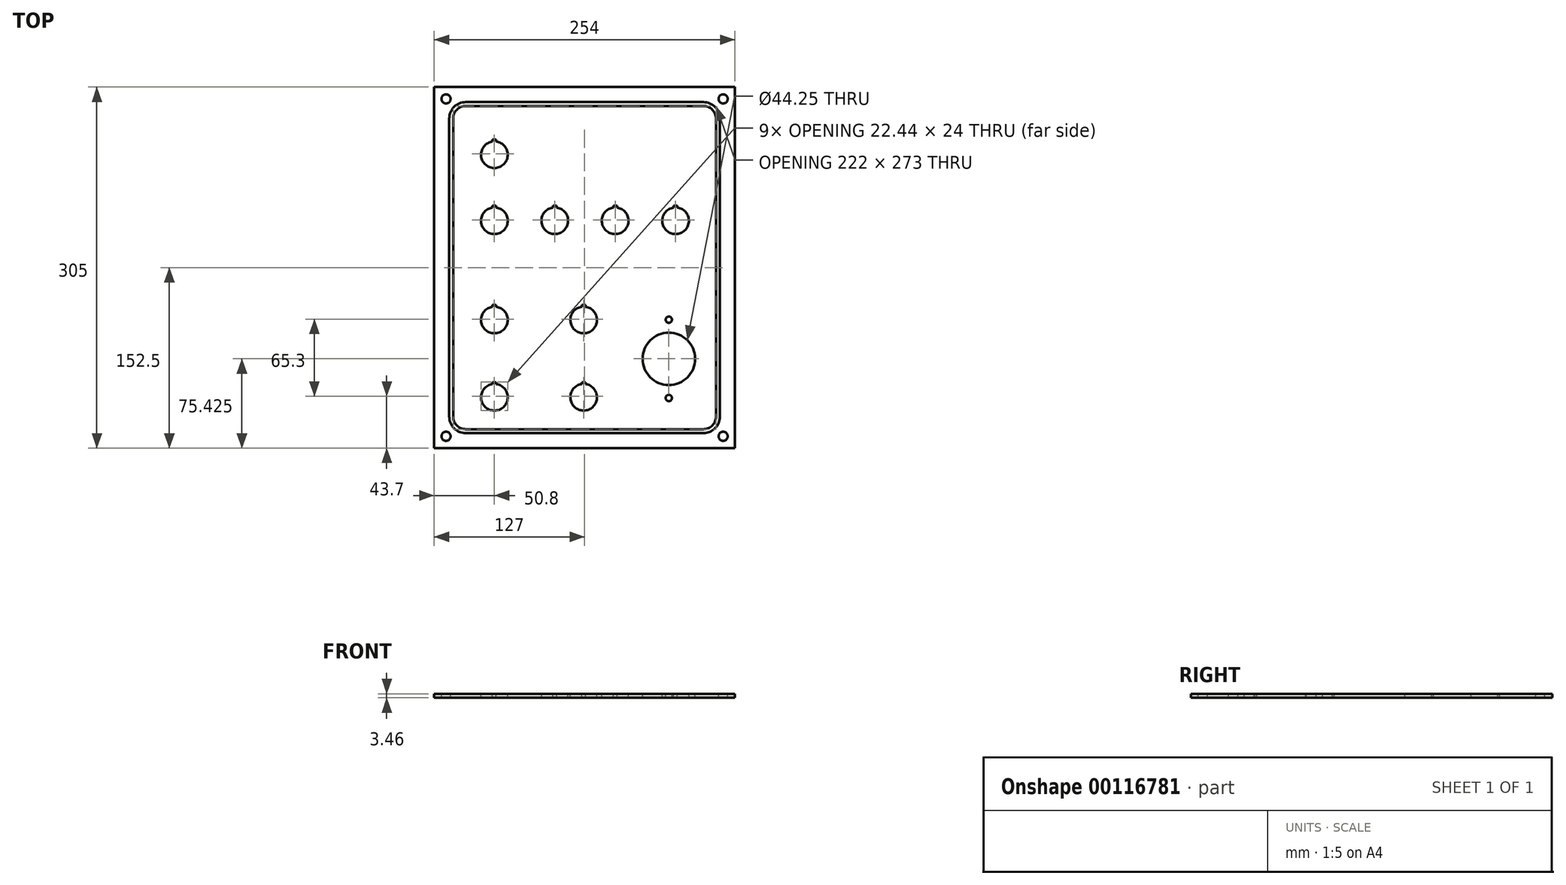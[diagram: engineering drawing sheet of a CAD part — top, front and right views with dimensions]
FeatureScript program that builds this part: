
annotation { "Feature Type Name" : "Feature", "Feature Type Description" : "" }
export const myFeature = defineFeature(function(context is Context, id is Id, definition is map)
    precondition{}
    {
        {
            var Q0;
            Q0=qCreatedBy(makeId("Top.planeOp"),FACE);
            var sketch = newSketch(context, id + "F0", { "sketchPlane" : qUnion([Q0])});
            skLineSegment(sketch, "E0.bottom", {"start": v(0, 0) * mm, "end": v(254, 0) * mm});
            skLineSegment(sketch, "E0.top", {"start": v(0, 305) * mm, "end": v(254, 305) * mm});
            skLineSegment(sketch, "E0.left", {"start": v(0, 0) * mm, "end": v(0, 305) * mm});
            skLineSegment(sketch, "E0.right", {"start": v(254, 0) * mm, "end": v(254, 305) * mm});
            skLineSegment(sketch, "E1.bottom", {"start": v(26.7, 292.3) * mm, "end": v(227.3, 292.3) * mm});
            skLineSegment(sketch, "E1.top", {"start": v(26.7, 12.7) * mm, "end": v(227.3, 12.7) * mm});
            skLineSegment(sketch, "E1.left", {"start": v(12.7, 278.3) * mm, "end": v(12.7, 26.7) * mm});
            skLineSegment(sketch, "E1.right", {"start": v(241.3, 278.3) * mm, "end": v(241.3, 26.7) * mm});
            skLineSegment(sketch, "E2.bottom", {"start": v(26.7, 16) * mm, "end": v(227.3, 16) * mm});
            skLineSegment(sketch, "E2.top", {"start": v(26.7, 289) * mm, "end": v(227.3, 289) * mm});
            skLineSegment(sketch, "E2.left", {"start": v(16, 26.7) * mm, "end": v(16, 278.3) * mm});
            skLineSegment(sketch, "E2.right", {"start": v(238, 26.7) * mm, "end": v(238, 278.3) * mm});
            skPoint(sketch, "E3.visualSharp", {"position": v(12.7, 292.3) * mm});
            skArc(sketch, "E3.filletArc", {"start": v(26.7, 292.3) * mm, "mid": v(16.8, 288.2) * mm, "end": v(12.7, 278.3) * mm});
            skPoint(sketch, "E4.visualSharp", {"position": v(241.3, 292.3) * mm});
            skArc(sketch, "E4.filletArc", {"start": v(241.3, 278.3) * mm, "mid": v(237.2, 288.2) * mm, "end": v(227.3, 292.3) * mm});
            skPoint(sketch, "E5.visualSharp", {"position": v(241.3, 12.7) * mm});
            skArc(sketch, "E5.filletArc", {"start": v(227.3, 12.7) * mm, "mid": v(237.2, 16.8) * mm, "end": v(241.3, 26.7) * mm});
            skPoint(sketch, "E6.visualSharp", {"position": v(12.7, 12.7) * mm});
            skArc(sketch, "E6.filletArc", {"start": v(12.7, 26.7) * mm, "mid": v(16.8, 16.8) * mm, "end": v(26.7, 12.7) * mm});
            skPoint(sketch, "E7.visualSharp", {"position": v(16, 289) * mm});
            skArc(sketch, "E7.filletArc", {"start": v(26.7, 289) * mm, "mid": v(19.13, 285.87) * mm, "end": v(16, 278.3) * mm});
            skPoint(sketch, "E8.visualSharp", {"position": v(238, 289) * mm});
            skArc(sketch, "E8.filletArc", {"start": v(238, 278.3) * mm, "mid": v(234.87, 285.87) * mm, "end": v(227.3, 289) * mm});
            skPoint(sketch, "E9.visualSharp", {"position": v(238, 16) * mm});
            skArc(sketch, "E9.filletArc", {"start": v(227.3, 16) * mm, "mid": v(234.87, 19.13) * mm, "end": v(238, 26.7) * mm});
            skPoint(sketch, "E10.visualSharp", {"position": v(16, 16) * mm});
            skArc(sketch, "E10.filletArc", {"start": v(16, 26.7) * mm, "mid": v(19.13, 19.13) * mm, "end": v(26.7, 16) * mm});
            skSolve(sketch);
        }
        {
            var Q0;
            Q0=makeQuery(id+"F0.imprint","IMPRINT",FACE,{"disambiguationData":[TD([[makeQuery(id+"F0.imprint","IMPRINT",EDGE,{"derivedFrom":sQuery(id+"F0.wireOp",EDGE,"E0.bottom")}),1.0]])]});
            var Q1;
            Q1=makeQuery(id+"F0.imprint","IMPRINT",FACE,{"disambiguationData":[TD([[makeQuery(id+"F0.imprint","IMPRINT",EDGE,{"derivedFrom":sQuery(id+"F0.wireOp",EDGE,"E1.bottom")}),-1.0]])]});
            var Q2;
            Q2=makeQuery(id+"F0.imprint","IMPRINT",FACE,{"disambiguationData":[TD([[makeQuery(id+"F0.imprint","IMPRINT",EDGE,{"derivedFrom":sQuery(id+"F0.wireOp",EDGE,"E2.bottom")}),1.0]])]});
            extrude(context, id + "F1", {"entities" : qUnion([Q0, Q1, Q2]), "oppositeDirection" : true, "depth" : 3.45 * mm, "offsetDistance" : 25 * mm});
        }
        {
            var Q0;
            Q0=makeQuery(id+"F0.imprint","IMPRINT",FACE,{"disambiguationData":[TD([[makeQuery(id+"F0.imprint","IMPRINT",EDGE,{"derivedFrom":sQuery(id+"F0.wireOp",EDGE,"E1.bottom")}),-1.0]])]});
            extrude(context, id + "F2", {"entities" : qUnion([Q0]), "depth" : 0.01 * mm, "offsetDistance" : 25 * mm});
        }
        {
            var Q0;
            Q0=makeQuery(id+"F0.imprint","IMPRINT",FACE,{"disambiguationData":[TD([[makeQuery(id+"F0.imprint","IMPRINT",EDGE,{"derivedFrom":sQuery(id+"F0.wireOp",EDGE,"E0.bottom")}),1.0]])]});
            var sketch = newSketch(context, id + "F3", { "sketchPlane" : qUnion([Q0])});
            skCircle(sketch, "E11", {"center": v(10, 10) * mm, "radius": 3.85 * mm});
            skCircle(sketch, "E12", {"center": v(10, 295) * mm, "radius": 3.85 * mm});
            skCircle(sketch, "E13", {"center": v(244, 295) * mm, "radius": 3.85 * mm});
            skCircle(sketch, "E14", {"center": v(244, 10) * mm, "radius": 3.85 * mm});
            skSolve(sketch);
        }
        {
            var Q0;
            Q0=makeQuery(id+"F3.imprint","IMPRINT",FACE,{"disambiguationData":[TD([[makeQuery(id+"F3.imprint","IMPRINT",EDGE,{"derivedFrom":sQuery(id+"F3.wireOp",EDGE,"E14")}),1.0]])]});
            var Q1;
            Q1=makeQuery(id+"F3.imprint","IMPRINT",FACE,{"disambiguationData":[TD([[makeQuery(id+"F3.imprint","IMPRINT",EDGE,{"derivedFrom":sQuery(id+"F3.wireOp",EDGE,"E11")}),1.0]])]});
            var Q2;
            Q2=makeQuery(id+"F3.imprint","IMPRINT",FACE,{"disambiguationData":[TD([[makeQuery(id+"F3.imprint","IMPRINT",EDGE,{"derivedFrom":sQuery(id+"F3.wireOp",EDGE,"E13")}),1.0]])]});
            var Q3;
            Q3=makeQuery(id+"F3.imprint","IMPRINT",FACE,{"disambiguationData":[TD([[makeQuery(id+"F3.imprint","IMPRINT",EDGE,{"derivedFrom":sQuery(id+"F3.wireOp",EDGE,"E12")}),1.0]])]});
            var Q4;
            Q4=sQuery(id+"F3.wireOp",EDGE,"E11");
            var Q5;
            Q5=sQuery(id+"F3.wireOp",EDGE,"E14");
            var Q6;
            Q6=sQuery(id+"F3.wireOp",EDGE,"E13");
            var Q7;
            Q7=sQuery(id+"F3.wireOp",EDGE,"E12");
            extrude(context, id + "F4", {"entities" : qUnion([Q0, Q1, Q2, Q3]), "operationType" : NewBodyOperationType.REMOVE, "surfaceEntities" : qUnion([Q4, Q5, Q6, Q7]), "endBound" : BoundingType.THROUGH_ALL, "oppositeDirection" : true, "depth" : 25 * mm, "offsetDistance" : 25 * mm});
        }
        {
            var Q0;
            Q0=makeQuery(id+"F3.imprint","IMPRINT",FACE,{"disambiguationData":[TD([[makeQuery(id+"F3.imprint","IMPRINT",EDGE,{"derivedFrom":makeQuery(id+"F0.imprint","IMPRINT",EDGE,{"derivedFrom":sQuery(id+"F0.wireOp",EDGE,"E1.bottom")})}),-1.0]])]});
            var sketch = newSketch(context, id + "F5", { "sketchPlane" : qUnion([Q0])});
            skCircle(sketch, "E15", {"center": v(50.8, 247.85) * mm, "radius": 11.25 * mm});
            skLineSegment(sketch, "E16.bottom", {"start": v(52.4, 257.6) * mm, "end": v(49.2, 257.6) * mm});
            skLineSegment(sketch, "E16.top", {"start": v(52.4, 260.6) * mm, "end": v(49.2, 260.6) * mm});
            skLineSegment(sketch, "E16.left", {"start": v(52.4, 257.6) * mm, "end": v(52.4, 260.6) * mm});
            skLineSegment(sketch, "E16.right", {"start": v(49.2, 257.6) * mm, "end": v(49.2, 260.6) * mm});
            skPoint(sketch, "E16.middle", {"position": v(50.8, 259.1) * mm});
            skSolve(sketch);
        }
        {
            var Q0;
            {var subQ5=sQuery(id+"F5.wireOp",EDGE,"E16.top");Q0=makeQuery(id+"F5.imprint","IMPRINT",FACE,{"disambiguationData":[TD([[makeQuery(id+"F5.imprint","IMPRINT",EDGE,{"derivedFrom":subQ5}),1.0]])]});}
            var Q1;
            {var subQ5=sQuery(id+"F5.wireOp",EDGE,"E16.bottom");Q1=makeQuery(id+"F5.imprint","IMPRINT",FACE,{"disambiguationData":[TD([[makeQuery(id+"F5.imprint","IMPRINT",EDGE,{"derivedFrom":subQ5}),-1.0]])]});}
            var Q2;
            {var subQ5=sQuery(id+"F5.wireOp",EDGE,"E16.bottom");Q2=makeQuery(id+"F5.imprint","IMPRINT",FACE,{"disambiguationData":[TD([[makeQuery(id+"F5.imprint","IMPRINT",EDGE,{"derivedFrom":subQ5}),1.0]])]});}
            extrude(context, id + "F6", {"entities" : qUnion([Q0, Q1, Q2]), "operationType" : NewBodyOperationType.REMOVE, "oppositeDirection" : true, "depth" : 25 * mm, "offsetDistance" : 25 * mm});
        }
        {
            var Q0;
            Q0=makeQuery(id+"F0.imprint","IMPRINT",FACE,{"disambiguationData":[TD([[makeQuery(id+"F0.imprint","IMPRINT",EDGE,{"derivedFrom":sQuery(id+"F0.wireOp",EDGE,"E2.bottom")}),1.0]])]});
            var sketch = newSketch(context, id + "F7", { "sketchPlane" : qUnion([Q0])});
            skCircle(sketch, "E17", {"center": v(50.8, 192.05) * mm, "radius": 11.25 * mm});
            skLineSegment(sketch, "E18.bottom", {"start": v(52.4, 201.8) * mm, "end": v(49.2, 201.8) * mm});
            skLineSegment(sketch, "E18.top", {"start": v(52.4, 204.8) * mm, "end": v(49.2, 204.8) * mm});
            skLineSegment(sketch, "E18.left", {"start": v(52.4, 201.8) * mm, "end": v(52.4, 204.8) * mm});
            skLineSegment(sketch, "E18.right", {"start": v(49.2, 201.8) * mm, "end": v(49.2, 204.8) * mm});
            skPoint(sketch, "E18.middle", {"position": v(50.8, 203.3) * mm});
            skPoint(sketch, "E19.1.0.0", {"position": v(101.8, 203.3) * mm});
            skCircle(sketch, "E19.1.0.1", {"center": v(101.8, 192.05) * mm, "radius": 11.25 * mm});
            skLineSegment(sketch, "E19.1.0.2", {"start": v(103.4, 204.8) * mm, "end": v(100.2, 204.8) * mm});
            skLineSegment(sketch, "E19.1.0.3", {"start": v(100.2, 201.8) * mm, "end": v(100.2, 204.8) * mm});
            skLineSegment(sketch, "E19.1.0.4", {"start": v(103.4, 201.8) * mm, "end": v(103.4, 204.8) * mm});
            skLineSegment(sketch, "E19.1.0.5", {"start": v(103.4, 201.8) * mm, "end": v(100.2, 201.8) * mm});
            skPoint(sketch, "E19.2.0.0", {"position": v(152.8, 203.3) * mm});
            skCircle(sketch, "E19.2.0.1", {"center": v(152.8, 192.05) * mm, "radius": 11.25 * mm});
            skLineSegment(sketch, "E19.2.0.2", {"start": v(154.4, 204.8) * mm, "end": v(151.2, 204.8) * mm});
            skLineSegment(sketch, "E19.2.0.3", {"start": v(151.2, 201.8) * mm, "end": v(151.2, 204.8) * mm});
            skLineSegment(sketch, "E19.2.0.4", {"start": v(154.4, 201.8) * mm, "end": v(154.4, 204.8) * mm});
            skLineSegment(sketch, "E19.2.0.5", {"start": v(154.4, 201.8) * mm, "end": v(151.2, 201.8) * mm});
            skPoint(sketch, "E19.3.0.0", {"position": v(203.8, 203.3) * mm});
            skCircle(sketch, "E19.3.0.1", {"center": v(203.8, 192.05) * mm, "radius": 11.25 * mm});
            skLineSegment(sketch, "E19.3.0.2", {"start": v(205.4, 204.8) * mm, "end": v(202.2, 204.8) * mm});
            skLineSegment(sketch, "E19.3.0.3", {"start": v(202.2, 201.8) * mm, "end": v(202.2, 204.8) * mm});
            skLineSegment(sketch, "E19.3.0.4", {"start": v(205.4, 201.8) * mm, "end": v(205.4, 204.8) * mm});
            skLineSegment(sketch, "E19.3.0.5", {"start": v(205.4, 201.8) * mm, "end": v(202.2, 201.8) * mm});
            skLineSegment(sketch, "E19.direction1", {"start": v(50.8, 192.05) * mm, "end": v(101.8, 192.05) * mm, "construction": true});
            skSolve(sketch);
        }
        {
            var Q0;
            {var subQ5=sQuery(id+"F7.wireOp",EDGE,"E18.bottom");Q0=makeQuery(id+"F7.imprint","IMPRINT",FACE,{"disambiguationData":[TD([[makeQuery(id+"F7.imprint","IMPRINT",EDGE,{"derivedFrom":subQ5}),-1.0]])]});}
            var Q1;
            {var subQ5=sQuery(id+"F7.wireOp",EDGE,"E18.top");Q1=makeQuery(id+"F7.imprint","IMPRINT",FACE,{"disambiguationData":[TD([[makeQuery(id+"F7.imprint","IMPRINT",EDGE,{"derivedFrom":subQ5}),1.0]])]});}
            var Q2;
            {var subQ5=sQuery(id+"F7.wireOp",EDGE,"E19.1.0.2");Q2=makeQuery(id+"F7.imprint","IMPRINT",FACE,{"disambiguationData":[TD([[makeQuery(id+"F7.imprint","IMPRINT",EDGE,{"derivedFrom":subQ5}),1.0]])]});}
            var Q3;
            {var subQ5=sQuery(id+"F7.wireOp",EDGE,"E19.1.0.5");Q3=makeQuery(id+"F7.imprint","IMPRINT",FACE,{"disambiguationData":[TD([[makeQuery(id+"F7.imprint","IMPRINT",EDGE,{"derivedFrom":subQ5}),-1.0]])]});}
            var Q4;
            {var subQ5=sQuery(id+"F7.wireOp",EDGE,"E19.1.0.5");Q4=makeQuery(id+"F7.imprint","IMPRINT",FACE,{"disambiguationData":[TD([[makeQuery(id+"F7.imprint","IMPRINT",EDGE,{"derivedFrom":subQ5}),1.0]])]});}
            var Q5;
            {var subQ5=sQuery(id+"F7.wireOp",EDGE,"E18.bottom");Q5=makeQuery(id+"F7.imprint","IMPRINT",FACE,{"disambiguationData":[TD([[makeQuery(id+"F7.imprint","IMPRINT",EDGE,{"derivedFrom":subQ5}),1.0]])]});}
            var Q6;
            {var subQ5=sQuery(id+"F7.wireOp",EDGE,"E19.2.0.2");Q6=makeQuery(id+"F7.imprint","IMPRINT",FACE,{"disambiguationData":[TD([[makeQuery(id+"F7.imprint","IMPRINT",EDGE,{"derivedFrom":subQ5}),1.0]])]});}
            var Q7;
            {var subQ5=sQuery(id+"F7.wireOp",EDGE,"E19.2.0.5");Q7=makeQuery(id+"F7.imprint","IMPRINT",FACE,{"disambiguationData":[TD([[makeQuery(id+"F7.imprint","IMPRINT",EDGE,{"derivedFrom":subQ5}),-1.0]])]});}
            var Q8;
            {var subQ5=sQuery(id+"F7.wireOp",EDGE,"E19.2.0.5");Q8=makeQuery(id+"F7.imprint","IMPRINT",FACE,{"disambiguationData":[TD([[makeQuery(id+"F7.imprint","IMPRINT",EDGE,{"derivedFrom":subQ5}),1.0]])]});}
            var Q9;
            {var subQ5=sQuery(id+"F7.wireOp",EDGE,"E19.3.0.2");Q9=makeQuery(id+"F7.imprint","IMPRINT",FACE,{"disambiguationData":[TD([[makeQuery(id+"F7.imprint","IMPRINT",EDGE,{"derivedFrom":subQ5}),1.0]])]});}
            var Q10;
            {var subQ5=sQuery(id+"F7.wireOp",EDGE,"E19.3.0.5");Q10=makeQuery(id+"F7.imprint","IMPRINT",FACE,{"disambiguationData":[TD([[makeQuery(id+"F7.imprint","IMPRINT",EDGE,{"derivedFrom":subQ5}),-1.0]])]});}
            var Q11;
            {var subQ5=sQuery(id+"F7.wireOp",EDGE,"E19.3.0.5");Q11=makeQuery(id+"F7.imprint","IMPRINT",FACE,{"disambiguationData":[TD([[makeQuery(id+"F7.imprint","IMPRINT",EDGE,{"derivedFrom":subQ5}),1.0]])]});}
            extrude(context, id + "F8", {"entities" : qUnion([Q0, Q1, Q2, Q3, Q4, Q5, Q6, Q7, Q8, Q9, Q10, Q11]), "operationType" : NewBodyOperationType.REMOVE, "oppositeDirection" : true, "depth" : 25 * mm, "offsetDistance" : 25 * mm});
        }
        {
            var Q0;
            Q0=makeQuery(id+"F3.imprint","IMPRINT",FACE,{"disambiguationData":[TD([[makeQuery(id+"F3.imprint","IMPRINT",EDGE,{"derivedFrom":makeQuery(id+"F0.imprint","IMPRINT",EDGE,{"derivedFrom":sQuery(id+"F0.wireOp",EDGE,"E1.bottom")})}),-1.0]])]});
            var sketch = newSketch(context, id + "F9", { "sketchPlane" : qUnion([Q0])});
            skCircle(sketch, "E20", {"center": v(50.8, 108.25) * mm, "radius": 11.25 * mm});
            skLineSegment(sketch, "E21.bottom", {"start": v(52.4, 118) * mm, "end": v(49.2, 118) * mm});
            skLineSegment(sketch, "E21.top", {"start": v(52.4, 121) * mm, "end": v(49.2, 121) * mm});
            skLineSegment(sketch, "E21.left", {"start": v(52.4, 118) * mm, "end": v(52.4, 121) * mm});
            skLineSegment(sketch, "E21.right", {"start": v(49.2, 118) * mm, "end": v(49.2, 121) * mm});
            skPoint(sketch, "E21.middle", {"position": v(50.8, 119.5) * mm});
            skCircle(sketch, "E22.0.1.0", {"center": v(50.8, 42.95) * mm, "radius": 11.25 * mm});
            skLineSegment(sketch, "E22.0.1.1", {"start": v(52.4, 55.7) * mm, "end": v(49.2, 55.7) * mm});
            skPoint(sketch, "E22.0.1.2", {"position": v(50.8, 54.2) * mm});
            skLineSegment(sketch, "E22.0.1.3", {"start": v(52.4, 52.7) * mm, "end": v(49.2, 52.7) * mm});
            skLineSegment(sketch, "E22.0.1.4", {"start": v(52.4, 52.7) * mm, "end": v(52.4, 55.7) * mm});
            skLineSegment(sketch, "E22.0.1.5", {"start": v(49.2, 52.7) * mm, "end": v(49.2, 55.7) * mm});
            skCircle(sketch, "E22.1.0.0", {"center": v(126.2, 108.25) * mm, "radius": 11.25 * mm});
            skLineSegment(sketch, "E22.1.0.1", {"start": v(127.8, 121) * mm, "end": v(124.6, 121) * mm});
            skPoint(sketch, "E22.1.0.2", {"position": v(126.2, 119.5) * mm});
            skLineSegment(sketch, "E22.1.0.3", {"start": v(127.8, 118) * mm, "end": v(124.6, 118) * mm});
            skLineSegment(sketch, "E22.1.0.4", {"start": v(127.8, 118) * mm, "end": v(127.8, 121) * mm});
            skLineSegment(sketch, "E22.1.0.5", {"start": v(124.6, 118) * mm, "end": v(124.6, 121) * mm});
            skCircle(sketch, "E22.1.1.0", {"center": v(126.2, 42.95) * mm, "radius": 11.25 * mm});
            skLineSegment(sketch, "E22.1.1.1", {"start": v(127.8, 55.7) * mm, "end": v(124.6, 55.7) * mm});
            skPoint(sketch, "E22.1.1.2", {"position": v(126.2, 54.2) * mm});
            skLineSegment(sketch, "E22.1.1.3", {"start": v(127.8, 52.7) * mm, "end": v(124.6, 52.7) * mm});
            skLineSegment(sketch, "E22.1.1.4", {"start": v(127.8, 52.7) * mm, "end": v(127.8, 55.7) * mm});
            skLineSegment(sketch, "E22.1.1.5", {"start": v(124.6, 52.7) * mm, "end": v(124.6, 55.7) * mm});
            skLineSegment(sketch, "E22.direction1", {"start": v(50.8, 108.25) * mm, "end": v(126.2, 108.25) * mm, "construction": true});
            skLineSegment(sketch, "E22.direction2", {"start": v(50.8, 108.25) * mm, "end": v(50.8, 42.95) * mm, "construction": true});
            skSolve(sketch);
        }
        {
            var Q0;
            {var subQ5=sQuery(id+"F9.wireOp",EDGE,"E21.top");Q0=makeQuery(id+"F9.imprint","IMPRINT",FACE,{"disambiguationData":[TD([[makeQuery(id+"F9.imprint","IMPRINT",EDGE,{"derivedFrom":subQ5}),1.0]])]});}
            var Q1;
            {var subQ5=sQuery(id+"F9.wireOp",EDGE,"E21.bottom");Q1=makeQuery(id+"F9.imprint","IMPRINT",FACE,{"disambiguationData":[TD([[makeQuery(id+"F9.imprint","IMPRINT",EDGE,{"derivedFrom":subQ5}),-1.0]])]});}
            var Q2;
            {var subQ5=sQuery(id+"F9.wireOp",EDGE,"E21.bottom");Q2=makeQuery(id+"F9.imprint","IMPRINT",FACE,{"disambiguationData":[TD([[makeQuery(id+"F9.imprint","IMPRINT",EDGE,{"derivedFrom":subQ5}),1.0]])]});}
            var Q3;
            {var subQ5=sQuery(id+"F9.wireOp",EDGE,"E22.1.0.1");Q3=makeQuery(id+"F9.imprint","IMPRINT",FACE,{"disambiguationData":[TD([[makeQuery(id+"F9.imprint","IMPRINT",EDGE,{"derivedFrom":subQ5}),1.0]])]});}
            var Q4;
            {var subQ5=sQuery(id+"F9.wireOp",EDGE,"E22.1.0.3");Q4=makeQuery(id+"F9.imprint","IMPRINT",FACE,{"disambiguationData":[TD([[makeQuery(id+"F9.imprint","IMPRINT",EDGE,{"derivedFrom":subQ5}),-1.0]])]});}
            var Q5;
            {var subQ5=sQuery(id+"F9.wireOp",EDGE,"E22.1.0.3");Q5=makeQuery(id+"F9.imprint","IMPRINT",FACE,{"disambiguationData":[TD([[makeQuery(id+"F9.imprint","IMPRINT",EDGE,{"derivedFrom":subQ5}),1.0]])]});}
            var Q6;
            {var subQ5=sQuery(id+"F9.wireOp",EDGE,"E22.1.1.1");Q6=makeQuery(id+"F9.imprint","IMPRINT",FACE,{"disambiguationData":[TD([[makeQuery(id+"F9.imprint","IMPRINT",EDGE,{"derivedFrom":subQ5}),1.0]])]});}
            var Q7;
            {var subQ5=sQuery(id+"F9.wireOp",EDGE,"E22.1.1.3");Q7=makeQuery(id+"F9.imprint","IMPRINT",FACE,{"disambiguationData":[TD([[makeQuery(id+"F9.imprint","IMPRINT",EDGE,{"derivedFrom":subQ5}),-1.0]])]});}
            var Q8;
            {var subQ5=sQuery(id+"F9.wireOp",EDGE,"E22.1.1.3");Q8=makeQuery(id+"F9.imprint","IMPRINT",FACE,{"disambiguationData":[TD([[makeQuery(id+"F9.imprint","IMPRINT",EDGE,{"derivedFrom":subQ5}),1.0]])]});}
            var Q9;
            {var subQ5=sQuery(id+"F9.wireOp",EDGE,"E22.0.1.1");Q9=makeQuery(id+"F9.imprint","IMPRINT",FACE,{"disambiguationData":[TD([[makeQuery(id+"F9.imprint","IMPRINT",EDGE,{"derivedFrom":subQ5}),1.0]])]});}
            var Q10;
            {var subQ5=sQuery(id+"F9.wireOp",EDGE,"E22.0.1.3");Q10=makeQuery(id+"F9.imprint","IMPRINT",FACE,{"disambiguationData":[TD([[makeQuery(id+"F9.imprint","IMPRINT",EDGE,{"derivedFrom":subQ5}),-1.0]])]});}
            var Q11;
            {var subQ5=sQuery(id+"F9.wireOp",EDGE,"E22.0.1.3");Q11=makeQuery(id+"F9.imprint","IMPRINT",FACE,{"disambiguationData":[TD([[makeQuery(id+"F9.imprint","IMPRINT",EDGE,{"derivedFrom":subQ5}),1.0]])]});}
            extrude(context, id + "F10", {"entities" : qUnion([Q0, Q1, Q2, Q3, Q4, Q5, Q6, Q7, Q8, Q9, Q10, Q11]), "operationType" : NewBodyOperationType.REMOVE, "oppositeDirection" : true, "depth" : 25 * mm, "offsetDistance" : 25 * mm});
        }
        {
            var Q0;
            Q0=makeQuery(id+"F1.opExtrude","CAP_FACE",FACE,{"disambiguationData":[OSD([sQuery(id+"F0.wireOp",EDGE,"E0.bottom"),sQuery(id+"F0.wireOp",EDGE,"E0.top"),sQuery(id+"F0.wireOp",EDGE,"E0.left"),sQuery(id+"F0.wireOp",EDGE,"E0.right")])],"isStart":true});
            var sketch = newSketch(context, id + "F11", { "sketchPlane" : qUnion([Q0])});
            skCircle(sketch, "E23", {"center": v(198.1, 75.42) * mm, "radius": 22.12 * mm});
            skCircle(sketch, "E24", {"center": v(198.1, 108.5) * mm, "radius": 2.65 * mm});
            skCircle(sketch, "E25", {"center": v(198.1, 42.35) * mm, "radius": 2.65 * mm});
            skSolve(sketch);
        }
        {
            var Q0;
            Q0=makeQuery(id+"F11.imprint","IMPRINT",FACE,{"disambiguationData":[TD([[makeQuery(id+"F11.imprint","IMPRINT",EDGE,{"derivedFrom":sQuery(id+"F11.wireOp",EDGE,"E24")}),1.0]])]});
            var Q1;
            Q1=makeQuery(id+"F11.imprint","IMPRINT",FACE,{"disambiguationData":[TD([[makeQuery(id+"F11.imprint","IMPRINT",EDGE,{"derivedFrom":sQuery(id+"F11.wireOp",EDGE,"E25")}),1.0]])]});
            var Q2;
            Q2=makeQuery(id+"F11.imprint","IMPRINT",FACE,{"disambiguationData":[TD([[makeQuery(id+"F11.imprint","IMPRINT",EDGE,{"derivedFrom":sQuery(id+"F11.wireOp",EDGE,"E23")}),1.0]])]});
            extrude(context, id + "F12", {"entities" : qUnion([Q0, Q1, Q2]), "operationType" : NewBodyOperationType.REMOVE, "oppositeDirection" : true, "depth" : 25 * mm, "offsetDistance" : 25 * mm});
        }
    });
